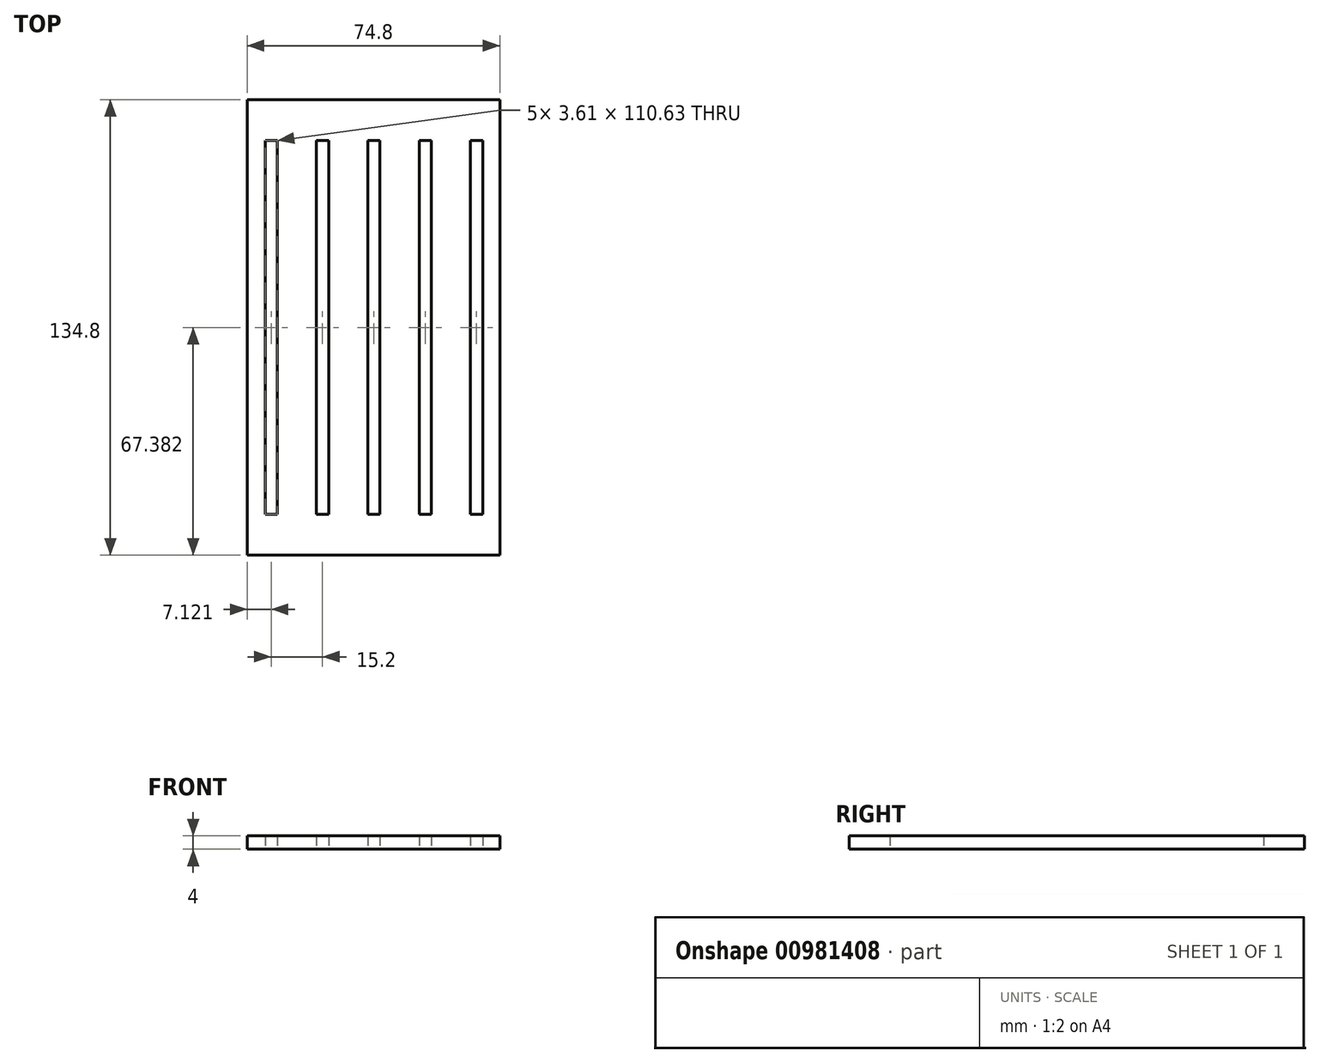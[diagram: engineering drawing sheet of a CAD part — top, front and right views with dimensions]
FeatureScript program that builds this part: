
annotation { "Feature Type Name" : "Feature", "Feature Type Description" : "" }
export const myFeature = defineFeature(function(context is Context, id is Id, definition is map)
    precondition{}
    {
        {
            var Q0;
            Q0=qCreatedBy(makeId("Top.planeOp"),FACE);
            var sketch = newSketch(context, id + "F0", { "sketchPlane" : qUnion([Q0])});
            skLineSegment(sketch, "E0.bottom", {"start": v(-37.4, -67.4) * mm, "end": v(37.4, -67.4) * mm});
            skLineSegment(sketch, "E0.top", {"start": v(-37.4, 67.4) * mm, "end": v(37.4, 67.4) * mm});
            skLineSegment(sketch, "E0.left", {"start": v(-37.4, -67.4) * mm, "end": v(-37.4, 67.4) * mm});
            skLineSegment(sketch, "E0.right", {"start": v(37.4, -67.4) * mm, "end": v(37.4, 67.4) * mm});
            skLineSegment(sketch, "E1.bottom", {"start": v(-32.08, 55.3) * mm, "end": v(-28.48, 55.3) * mm});
            skLineSegment(sketch, "E1.top", {"start": v(-32.08, -55.33) * mm, "end": v(-28.48, -55.33) * mm});
            skLineSegment(sketch, "E1.left", {"start": v(-32.08, 55.3) * mm, "end": v(-32.08, -55.33) * mm});
            skLineSegment(sketch, "E1.right", {"start": v(-28.48, 55.3) * mm, "end": v(-28.48, -55.33) * mm});
            skLineSegment(sketch, "E2.1.0.0", {"start": v(-13.28, 55.3) * mm, "end": v(-13.28, -55.33) * mm});
            skLineSegment(sketch, "E2.1.0.1", {"start": v(-16.88, 55.3) * mm, "end": v(-16.88, -55.33) * mm});
            skLineSegment(sketch, "E2.1.0.2", {"start": v(-16.88, -55.33) * mm, "end": v(-13.28, -55.33) * mm});
            skLineSegment(sketch, "E2.1.0.3", {"start": v(-16.88, 55.3) * mm, "end": v(-13.28, 55.3) * mm});
            skLineSegment(sketch, "E2.2.0.0", {"start": v(1.92, 55.3) * mm, "end": v(1.92, -55.33) * mm});
            skLineSegment(sketch, "E2.2.0.1", {"start": v(-1.68, 55.3) * mm, "end": v(-1.68, -55.33) * mm});
            skLineSegment(sketch, "E2.2.0.2", {"start": v(-1.68, -55.33) * mm, "end": v(1.92, -55.33) * mm});
            skLineSegment(sketch, "E2.2.0.3", {"start": v(-1.68, 55.3) * mm, "end": v(1.92, 55.3) * mm});
            skLineSegment(sketch, "E2.3.0.0", {"start": v(17.12, 55.3) * mm, "end": v(17.12, -55.33) * mm});
            skLineSegment(sketch, "E2.3.0.1", {"start": v(13.52, 55.3) * mm, "end": v(13.52, -55.33) * mm});
            skLineSegment(sketch, "E2.3.0.2", {"start": v(13.52, -55.33) * mm, "end": v(17.12, -55.33) * mm});
            skLineSegment(sketch, "E2.3.0.3", {"start": v(13.52, 55.3) * mm, "end": v(17.12, 55.3) * mm});
            skLineSegment(sketch, "E2.4.0.0", {"start": v(32.32, 55.3) * mm, "end": v(32.32, -55.33) * mm});
            skLineSegment(sketch, "E2.4.0.1", {"start": v(28.72, 55.3) * mm, "end": v(28.72, -55.33) * mm});
            skLineSegment(sketch, "E2.4.0.2", {"start": v(28.72, -55.33) * mm, "end": v(32.32, -55.33) * mm});
            skLineSegment(sketch, "E2.4.0.3", {"start": v(28.72, 55.3) * mm, "end": v(32.32, 55.3) * mm});
            skLineSegment(sketch, "E2.direction1", {"start": v(-32.08, -55.33) * mm, "end": v(-16.88, -55.33) * mm, "construction": true});
            skSolve(sketch);
        }
        {
            var Q0;
            Q0=makeQuery(id+"F0.imprint","IMPRINT",FACE,{"disambiguationData":[TD([[makeQuery(id+"F0.imprint","IMPRINT",EDGE,{"derivedFrom":sQuery(id+"F0.wireOp",EDGE,"E0.bottom")}),1.0]])]});
            extrude(context, id + "F1", {"entities" : qUnion([Q0]), "depth" : 4 * mm, "offsetDistance" : 25 * mm});
        }
    });
